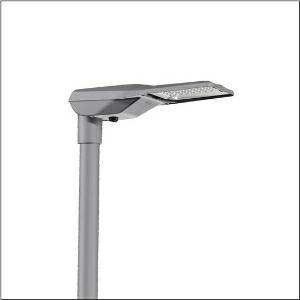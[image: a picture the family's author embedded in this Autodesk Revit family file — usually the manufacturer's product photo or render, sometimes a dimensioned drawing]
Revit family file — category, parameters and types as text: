
# Revit family: streetlight_sl_21_iq_mini___p0_8ab_5xe2r31u08hb_e37e
name_source: partatom
category: Lighting Fixtures
units: mm (PartAtom-declared; Revit-internal decimal feet)

## family parameters
Cut with Voids When Loaded = No
Host = Face
Light Source = No
Part Type = Normal
Room Calculation Point = No
Round Connector Dimension = Use Diameter
Shared = No

## types (1)
- --- (1 x LED, 8460 lm, 71 W, 3000K)
    Apparent Load = 71 VA
    CIE Flux Codes = 36 71 98 100 100
    Color Rendering = 70
    Color Temperature = 3000K
    Default Elevation = 1800 mm
    Description = Streetlight SL 21 iQ mini, mast luminaire, primary light control with lens, of PMMA, primary optical cover: cover, of toughened safety glass, transparent, light distribution: P0.8aB, light emission: direct distribution, primary light characteristic: asymmetric, installation type: post-top, side-entry, LED, High Power LED, rated luminous flux: 8.460lm, luminous efficacy: 119lm/W, light colour: 730, colour temperature: 3000K, control gear: iQ-Street Remote, D4i with power reduction, control: pre-setting: logarithmic dimming characteristic, Street-Remote, Auto-Match, Temp-Guard, Lumen-Switch, Night-Set, Smart-Wire, Light-Fading, Desk-Remote (wireless, voltage-free reading and setting of iQ features in the workshop via application-optimized NFC function/RFID function), optimised constant luminous flux control (CLO 2.0), mains connection: 220..240V, AC, 50/60Hz, start of lifetime: 71W, end of service life: 75W, reduction: 30W, luminaire housing, of diecast aluminium, powder-coated, Siteco® metallic grey (DB 702S), corrosivity category C5 mid according to DIN EN ISO 12944, please order mast flange separately, inclination adjustable: 0°, 5°, 10°, 15°, sealing non-destructively replaceable, multi-level sealing system, length: 628mm, width: 235mm, height: 110mm, mast flange for spigot size: 42mm (side-entry): 5XC10008XM4, 60/48mm (side-entry/post-top): 5XC10108XM2, 76/60mm (side-entry/post-top): 5XC10108XM1, mounting height: 4..8m, Smart Interface below, protection rating (complete): IP66, insulation class (complete): insulation class II (safety insulation), certification: CE, ENEC, ENEC+, VDE, impact resistance: IK10, permissible operating ambient temperature for outdoor applications: -40..+50°C, standard-compliant lighting for roads and squares, packaging unit: 1 piece

Light Distribution: P0.8aB
    Height = 110 mm
    Lamp = 1 x LED
    Lamp Light Flux = 8460 lm
    Lamp Power = 71 W
    Lamp count = 1
    Length = 625 mm
    Luminous efficacy = 119 lm/W
    Manufacturer = Siteco
    ModVariant = No
    Model = 5XE2R31U08HB
    Number of Poles = 1
    OnlyDefault = Yes
    Power Factor = 1
    Product Name = Streetlight SL 21 iQ mini | P0.8aB
    Product group = mast luminaire | pylon top
    ProductGroupID = 6100
    Protection Class = Protection class II
    Protection Degree = IP 66
    RLX_Detail_Level = 1
    RLX_Emergency_Light_Flux = 0 lm
    RLX_Emergency_Type = 0
    RLX_Emergency_Type_DB = No
    RlxData = <blob elided: 26213 chars, md5=3f866822>
    Socket = socket
    Standby Power = 0 W
    System Light Flux = 8460 lm
    System Power = 71 W
    Type Comments = factory setting: luminous flux: 100 % | dim-lin: 254 | 716 mA
    Type Image = l_1003516.jpg
    URL = http://relux.com
    VarID = @adj_075466
    Voltage = 0 V
    Weight = 0.00 kg
    Width = 234 mm

## geometry (parser evidence)
native form markers: Blend x4, Sweep x10
no freeform markers — native parametric forms only
